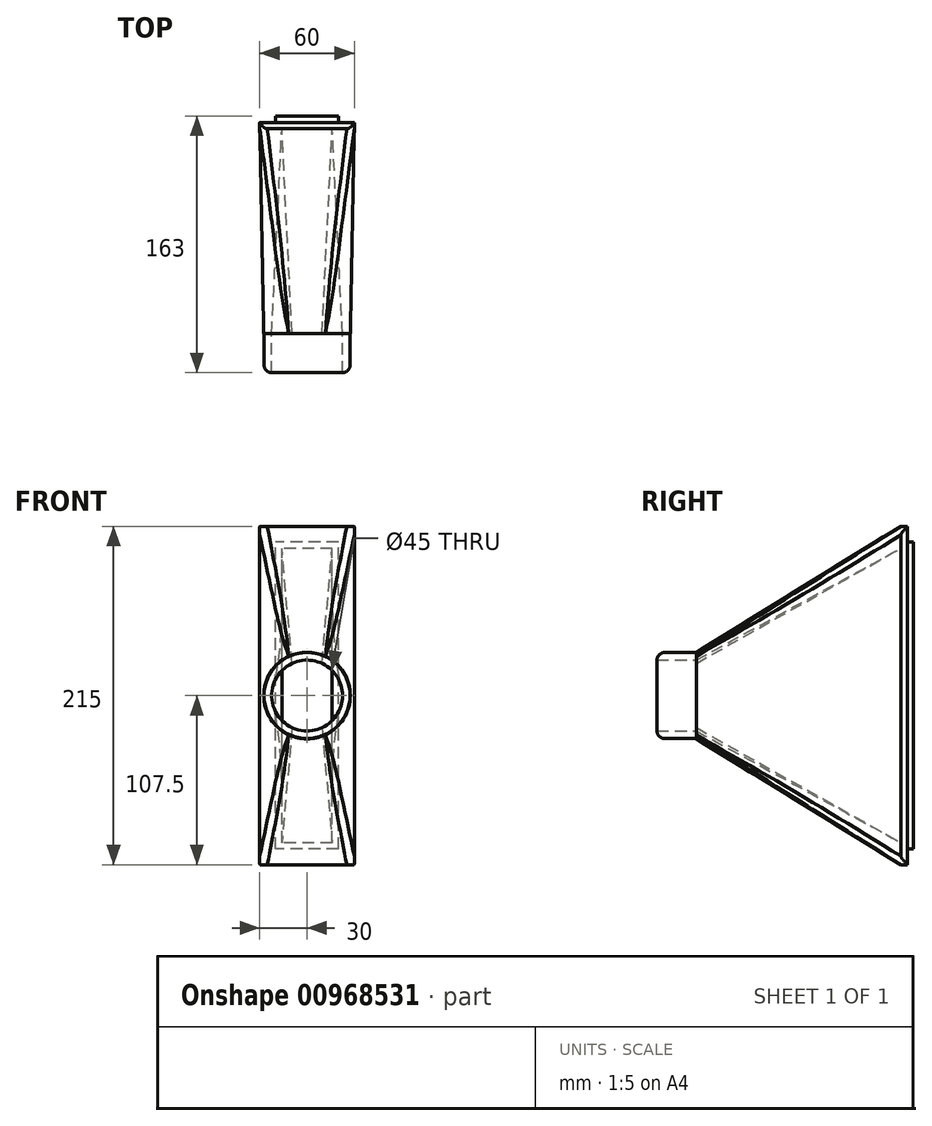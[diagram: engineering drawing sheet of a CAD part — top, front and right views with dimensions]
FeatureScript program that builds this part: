
annotation { "Feature Type Name" : "Feature", "Feature Type Description" : "" }
export const myFeature = defineFeature(function(context is Context, id is Id, definition is map)
    precondition{}
    {
        {
            var Q0;
            Q0=qCreatedBy(makeId("Front.planeOp"),FACE);
            var sketch = newSketch(context, id + "F0", { "sketchPlane" : qUnion([Q0])});
            skLineSegment(sketch, "E0.bottom", {"start": v(30, -107.5) * mm, "end": v(-30, -107.5) * mm});
            skLineSegment(sketch, "E0.top", {"start": v(30, 107.5) * mm, "end": v(-30, 107.5) * mm});
            skLineSegment(sketch, "E0.left", {"start": v(30, -107.5) * mm, "end": v(30, 107.5) * mm});
            skLineSegment(sketch, "E0.right", {"start": v(-30, -107.5) * mm, "end": v(-30, 107.5) * mm});
            skPoint(sketch, "E0.middle", {"position": v(0, 0) * mm});
            skLineSegment(sketch, "E1.0", {"start": v(20, 97.5) * mm, "end": v(-20, 97.5) * mm});
            skLineSegment(sketch, "E1.1", {"start": v(20, -97.5) * mm, "end": v(20, 97.5) * mm});
            skLineSegment(sketch, "E1.2", {"start": v(20, -97.5) * mm, "end": v(-20, -97.5) * mm});
            skLineSegment(sketch, "E1.3", {"start": v(-20, -97.5) * mm, "end": v(-20, 97.5) * mm});
            skLineSegment(sketch, "E2.0", {"start": v(16, 93.5) * mm, "end": v(-16, 93.5) * mm});
            skLineSegment(sketch, "E2.1", {"start": v(16, -93.5) * mm, "end": v(16, 93.5) * mm});
            skLineSegment(sketch, "E2.2", {"start": v(16, -93.5) * mm, "end": v(-16, -93.5) * mm});
            skLineSegment(sketch, "E2.3", {"start": v(-16, -93.5) * mm, "end": v(-16, 93.5) * mm});
            skSolve(sketch);
        }
        {
            var Q0;
            Q0=makeQuery(id+"F0.imprint","IMPRINT",FACE,{"disambiguationData":[TD([[makeQuery(id+"F0.imprint","IMPRINT",EDGE,{"derivedFrom":sQuery(id+"F0.wireOp",EDGE,"E1.0")}),1.0]])]});
            extrude(context, id + "F1", {"entities" : qUnion([Q0]), "oppositeDirection" : true, "depth" : 4 * mm, "offsetDistance" : 25 * mm});
        }
        {
            var Q0;
            Q0 = qSketchRegion(id + "F0", true);
            var Q1;
            Q1=makeQuery(id+"F1.opExtrude","CAP_FACE",FACE,{"disambiguationData":[OSD([sQuery(id+"F0.wireOp",EDGE,"E1.0"),sQuery(id+"F0.wireOp",EDGE,"E1.1"),sQuery(id+"F0.wireOp",EDGE,"E1.2"),sQuery(id+"F0.wireOp",EDGE,"E1.3"),sQuery(id+"F0.wireOp",EDGE,"E2.0"),sQuery(id+"F0.wireOp",EDGE,"E2.1"),sQuery(id+"F0.wireOp",EDGE,"E2.2"),sQuery(id+"F0.wireOp",EDGE,"E2.3")])],"isStart":true});
            extrude(context, id + "F2", {"entities" : qUnion([Q0, Q1]), "operationType" : NewBodyOperationType.ADD, "depth" : 4 * mm, "offsetDistance" : 25 * mm});
        }
        {
            var Q0;
            {var subQ0=sQuery(id+"F0.wireOp",EDGE,"E1.3");var subQ1=sQuery(id+"F0.wireOp",EDGE,"E1.2");var subQ2=sQuery(id+"F0.wireOp",EDGE,"E1.1");var subQ3=sQuery(id+"F0.wireOp",EDGE,"E1.0");Q0=makeQuery(id+"F2.boolean.opBoolean","MERGE",FACE,{"derivedFrom":[makeQuery(id+"F2.opExtrude","CAP_FACE",FACE,{"disambiguationData":[OSD([sQuery(id+"F0.wireOp",EDGE,"E0.bottom"),sQuery(id+"F0.wireOp",EDGE,"E0.top"),sQuery(id+"F0.wireOp",EDGE,"E0.left"),sQuery(id+"F0.wireOp",EDGE,"E0.right"),subQ3,subQ2,subQ1,subQ0])],"isStart":false}),makeQuery(id+"F2.opExtrude","CAP_FACE",FACE,{"disambiguationData":[OSD([subQ3,subQ2,subQ1,subQ0,sQuery(id+"F0.wireOp",EDGE,"E2.0"),sQuery(id+"F0.wireOp",EDGE,"E2.1"),sQuery(id+"F0.wireOp",EDGE,"E2.2"),sQuery(id+"F0.wireOp",EDGE,"E2.3")])],"isStart":false})]});}
            cPlane(context, id + "F3", {"entities" : qUnion([Q0]), "cplaneType" : CPlaneType.OFFSET, "offset" : 130 * mm, "width" : 150 * mm, "height" : 150 * mm});
        }
        {
            var Q0;
            {var subQ0=sQuery(id+"F0.wireOp",EDGE,"E1.3");var subQ1=sQuery(id+"F0.wireOp",EDGE,"E1.2");var subQ2=sQuery(id+"F0.wireOp",EDGE,"E1.1");var subQ3=sQuery(id+"F0.wireOp",EDGE,"E1.0");Q0=makeQuery(id+"F2.boolean.opBoolean","MERGE",FACE,{"derivedFrom":[makeQuery(id+"F2.opExtrude","CAP_FACE",FACE,{"disambiguationData":[OSD([sQuery(id+"F0.wireOp",EDGE,"E0.bottom"),sQuery(id+"F0.wireOp",EDGE,"E0.top"),sQuery(id+"F0.wireOp",EDGE,"E0.left"),sQuery(id+"F0.wireOp",EDGE,"E0.right"),subQ3,subQ2,subQ1,subQ0])],"isStart":false}),makeQuery(id+"F2.opExtrude","CAP_FACE",FACE,{"disambiguationData":[OSD([subQ3,subQ2,subQ1,subQ0,sQuery(id+"F0.wireOp",EDGE,"E2.0"),sQuery(id+"F0.wireOp",EDGE,"E2.1"),sQuery(id+"F0.wireOp",EDGE,"E2.2"),sQuery(id+"F0.wireOp",EDGE,"E2.3")])],"isStart":false})]});}
            var sketch = newSketch(context, id + "F4", { "sketchPlane" : qUnion([Q0])});
            skLineSegment(sketch, "E3", {"start": v(-16, 93.5) * mm, "end": v(-30, 107.5) * mm});
            skLineSegment(sketch, "E4", {"start": v(16, 93.5) * mm, "end": v(30, 107.5) * mm});
            skLineSegment(sketch, "E5", {"start": v(-16, -93.5) * mm, "end": v(-30, -107.5) * mm});
            skLineSegment(sketch, "E6", {"start": v(16, -93.5) * mm, "end": v(30, -107.5) * mm});
            skSolve(sketch);
        }
        {
            var Q0;
            Q0=qCreatedBy(id+"F3.planeOp",FACE);
            var sketch = newSketch(context, id + "F5", { "sketchPlane" : qUnion([Q0])});
            skCircle(sketch, "E7", {"center": v(0, 0) * mm, "radius": 27.5 * mm});
            skLineSegment(sketch, "E8.1.0", {"start": v(0, 0) * mm, "end": v(11.62, 24.92) * mm});
            skLineSegment(sketch, "E8.1.1", {"start": v(0, 0) * mm, "end": v(-11.62, -24.92) * mm});
            skLineSegment(sketch, "E8.anchor2", {"start": v(0, 0) * mm, "end": v(11.62, 24.92) * mm, "construction": true});
            skLineSegment(sketch, "E9.1.0", {"start": v(0, 0) * mm, "end": v(-11.62, 24.92) * mm, "construction": true});
            skLineSegment(sketch, "E9.1.1", {"start": v(0, 0) * mm, "end": v(9.5, -20.4) * mm});
            skLineSegment(sketch, "E9.anchor2", {"start": v(0, 0) * mm, "end": v(-9.5, 20.4) * mm, "construction": true});
            skLineSegment(sketch, "E10", {"start": v(9.5, -20.4) * mm, "end": v(9.5, -20.4) * mm});
            skLineSegment(sketch, "E11", {"start": v(11.62, -24.92) * mm, "end": v(11.62, -24.92) * mm});
            skLineSegment(sketch, "E12", {"start": v(-11.62, -24.92) * mm, "end": v(-11.62, -24.92) * mm});
            skLineSegment(sketch, "E13", {"start": v(9.5, -20.4) * mm, "end": v(11.62, -24.92) * mm});
            skArc(sketch, "E14", {"start": v(-9.5, -20.4) * mm, "mid": v(20.4, -9.5) * mm, "end": v(9.5, 20.4) * mm});
            skArc(sketch, "E15", {"start": v(9.5, 20.4) * mm, "mid": v(0, 22.5) * mm, "end": v(-9.5, 20.4) * mm});
            skLineSegment(sketch, "E16", {"start": v(11.62, 24.92) * mm, "end": v(11.62, 24.92) * mm});
            skArc(sketch, "E17", {"start": v(-9.5, 20.4) * mm, "mid": v(-22.5, 0) * mm, "end": v(-9.5, -20.4) * mm});
            skLineSegment(sketch, "E18", {"start": v(-11.62, 24.92) * mm, "end": v(-11.62, 24.92) * mm});
            skLineSegment(sketch, "E19", {"start": v(-9.5, 20.4) * mm, "end": v(-11.62, 24.92) * mm});
            skSolve(sketch);
        }
        {
            var Q1;
            {var subQ3=sQuery(id+"F5.wireOp",EDGE,"E13");Q1=makeQuery(id+"F5.imprint","IMPRINT",FACE,{"disambiguationData":[TD([[makeQuery(id+"F5.imprint","IMPRINT",EDGE,{"derivedFrom":subQ3}),-1.0]])]});}
            var Q2;
            Q2=makeQuery(id+"F4.imprint","IMPRINT",FACE,{"disambiguationData":[TD([[makeQuery(id+"F4.imprint","IMPRINT",EDGE,{"derivedFrom":sQuery(id+"F4.wireOp",EDGE,"E5")}),1.0]])]});
            loft(context, id + "F6", {"operationType" : NewBodyOperationType.ADD, "sheetProfilesArray" : [{ "sheetProfileEntities" : qUnion([Q1]) }, { "sheetProfileEntities" : qUnion([Q2]) }]});
        }
        {
            var Q1;
            {var subQ3=sQuery(id+"F5.wireOp",EDGE,"E13");Q1=makeQuery(id+"F5.imprint","IMPRINT",FACE,{"disambiguationData":[TD([[makeQuery(id+"F5.imprint","IMPRINT",EDGE,{"derivedFrom":subQ3}),1.0]])]});}
            var Q2;
            Q2=makeQuery(id+"F4.imprint","IMPRINT",FACE,{"disambiguationData":[TD([[makeQuery(id+"F4.imprint","IMPRINT",EDGE,{"derivedFrom":sQuery(id+"F4.wireOp",EDGE,"E4")}),-1.0]])]});
            loft(context, id + "F7", {"operationType" : NewBodyOperationType.ADD, "sheetProfilesArray" : [{ "sheetProfileEntities" : qUnion([Q1]) }, { "sheetProfileEntities" : qUnion([Q2]) }]});
        }
        {
            var Q1;
            {var subQ4=sQuery(id+"F5.wireOp",EDGE,"E17");Q1=makeQuery(id+"F5.imprint","IMPRINT",FACE,{"disambiguationData":[TD([[makeQuery(id+"F5.imprint","IMPRINT",EDGE,{"derivedFrom":subQ4}),-1.0]])]});}
            var Q2;
            Q2=makeQuery(id+"F4.imprint","IMPRINT",FACE,{"disambiguationData":[TD([[makeQuery(id+"F4.imprint","IMPRINT",EDGE,{"derivedFrom":sQuery(id+"F4.wireOp",EDGE,"E3")}),1.0]])]});
            loft(context, id + "F8", {"operationType" : NewBodyOperationType.ADD, "sheetProfilesArray" : [{ "sheetProfileEntities" : qUnion([Q1]) }, { "sheetProfileEntities" : qUnion([Q2]) }]});
        }
        {
            var Q1;
            {var subQ4=sQuery(id+"F5.wireOp",EDGE,"E15");Q1=makeQuery(id+"F5.imprint","IMPRINT",FACE,{"disambiguationData":[TD([[makeQuery(id+"F5.imprint","IMPRINT",EDGE,{"derivedFrom":subQ4}),-1.0]])]});}
            var Q2;
            Q2=makeQuery(id+"F4.imprint","IMPRINT",FACE,{"disambiguationData":[TD([[makeQuery(id+"F4.imprint","IMPRINT",EDGE,{"derivedFrom":sQuery(id+"F4.wireOp",EDGE,"E3")}),-1.0]])]});
            loft(context, id + "F9", {"operationType" : NewBodyOperationType.ADD, "sheetProfilesArray" : [{ "sheetProfileEntities" : qUnion([Q1]) }, { "sheetProfileEntities" : qUnion([Q2]) }]});
        }
        {
            var Q0;
            {var subQ4=sQuery(id+"F5.wireOp",EDGE,"E17");Q0=makeQuery(id+"F5.imprint","IMPRINT",FACE,{"disambiguationData":[TD([[makeQuery(id+"F5.imprint","IMPRINT",EDGE,{"derivedFrom":subQ4}),-1.0]])]});}
            cPlane(context, id + "F10", {"entities" : qUnion([Q0]), "cplaneType" : CPlaneType.OFFSET, "offset" : 0 * mm, "width" : 150 * mm, "height" : 150 * mm});
        }
        {
            var Q0;
            Q0=qCreatedBy(id+"F10.planeOp",FACE);
            var sketch = newSketch(context, id + "F11", { "sketchPlane" : qUnion([Q0])});
            skCircle(sketch, "E20", {"center": v(0, 0) * mm, "radius": 27.31 * mm});
            skCircle(sketch, "E21", {"center": v(0, 0) * mm, "radius": 22.5 * mm});
            skSolve(sketch);
        }
        {
            var Q0;
            Q0 = qSketchRegion(id + "F11", true);
            extrude(context, id + "F12", {"entities" : qUnion([Q0]), "operationType" : NewBodyOperationType.ADD, "depth" : 25 * mm, "offsetDistance" : 25 * mm});
        }
        {
            var Q0;
            Q0=makeQuery(id+"F12.opExtrude","CAP_EDGE",EDGE,{"disambiguationData":[OSD([sQuery(id+"F11.wireOp",EDGE,"E20")])],"isStart":false});
            var Q1;
            {var subQ0=sQuery(id+"F5.wireOp",EDGE,"E8.1.0");var subQ1=sQuery(id+"F5.wireOp",EDGE,"E7");var subQ2=sQuery(id+"F4.wireOp",EDGE,"E4");var subQ3=sQuery(id+"F0.wireOp",EDGE,"E0.left");var subQ4=sQuery(id+"F0.wireOp",EDGE,"E0.top");Q1=makeQuery(id+"F9.boolean.opBoolean","MERGE",EDGE,{"derivedFrom":[makeQuery(id+"F7.opLoft","SWEPT_EDGE",EDGE,{"disambiguationData":[OSD([subQ4,subQ3,subQ2,subQ1,subQ0])]}),makeQuery(id+"F9.opLoft","SWEPT_EDGE",EDGE,{"disambiguationData":[OSD([subQ4,subQ3,subQ2,subQ1,subQ0])]})]});}
            var Q2;
            {var subQ0=sQuery(id+"F5.wireOp",EDGE,"E19");var subQ1=sQuery(id+"F5.wireOp",EDGE,"E7");var subQ2=sQuery(id+"F4.wireOp",EDGE,"E3");var subQ3=sQuery(id+"F0.wireOp",EDGE,"E0.right");var subQ4=sQuery(id+"F0.wireOp",EDGE,"E0.top");Q2=makeQuery(id+"F9.boolean.opBoolean","MERGE",EDGE,{"derivedFrom":[makeQuery(id+"F8.opLoft","SWEPT_EDGE",EDGE,{"disambiguationData":[OSD([subQ4,subQ3,subQ2,subQ1,subQ0])]}),makeQuery(id+"F9.opLoft","SWEPT_EDGE",EDGE,{"disambiguationData":[OSD([subQ4,subQ3,subQ2,subQ1,subQ0])]})]});}
            var Q3;
            {var subQ0=sQuery(id+"F5.wireOp",EDGE,"E8.1.1");var subQ1=sQuery(id+"F5.wireOp",EDGE,"E7");var subQ2=sQuery(id+"F4.wireOp",EDGE,"E5");var subQ3=sQuery(id+"F0.wireOp",EDGE,"E0.right");var subQ4=sQuery(id+"F0.wireOp",EDGE,"E0.bottom");Q3=makeQuery(id+"F8.boolean.opBoolean","MERGE",EDGE,{"derivedFrom":[makeQuery(id+"F6.opLoft","SWEPT_EDGE",EDGE,{"disambiguationData":[OSD([subQ4,subQ3,subQ2,subQ1,subQ0])]}),makeQuery(id+"F8.opLoft","SWEPT_EDGE",EDGE,{"disambiguationData":[OSD([subQ4,subQ3,subQ2,subQ1,subQ0])]})]});}
            var Q4;
            {var subQ0=sQuery(id+"F5.wireOp",EDGE,"E13");var subQ1=sQuery(id+"F5.wireOp",EDGE,"E7");var subQ2=sQuery(id+"F4.wireOp",EDGE,"E6");var subQ3=sQuery(id+"F0.wireOp",EDGE,"E0.left");var subQ4=sQuery(id+"F0.wireOp",EDGE,"E0.bottom");Q4=makeQuery(id+"F7.boolean.opBoolean","MERGE",EDGE,{"derivedFrom":[makeQuery(id+"F6.opLoft","SWEPT_EDGE",EDGE,{"disambiguationData":[OSD([subQ4,subQ3,subQ2,subQ1,subQ0])]}),makeQuery(id+"F7.opLoft","SWEPT_EDGE",EDGE,{"disambiguationData":[OSD([subQ4,subQ3,subQ2,subQ1,subQ0])]})]});}
            fillet(context, id + "F13", {"entities" : qUnion([Q0, Q1, Q2, Q3, Q4]), "radius" : 5 * mm, "tangentPropagation" : true, "allowEdgeOverflow" : false});
        }
    });
